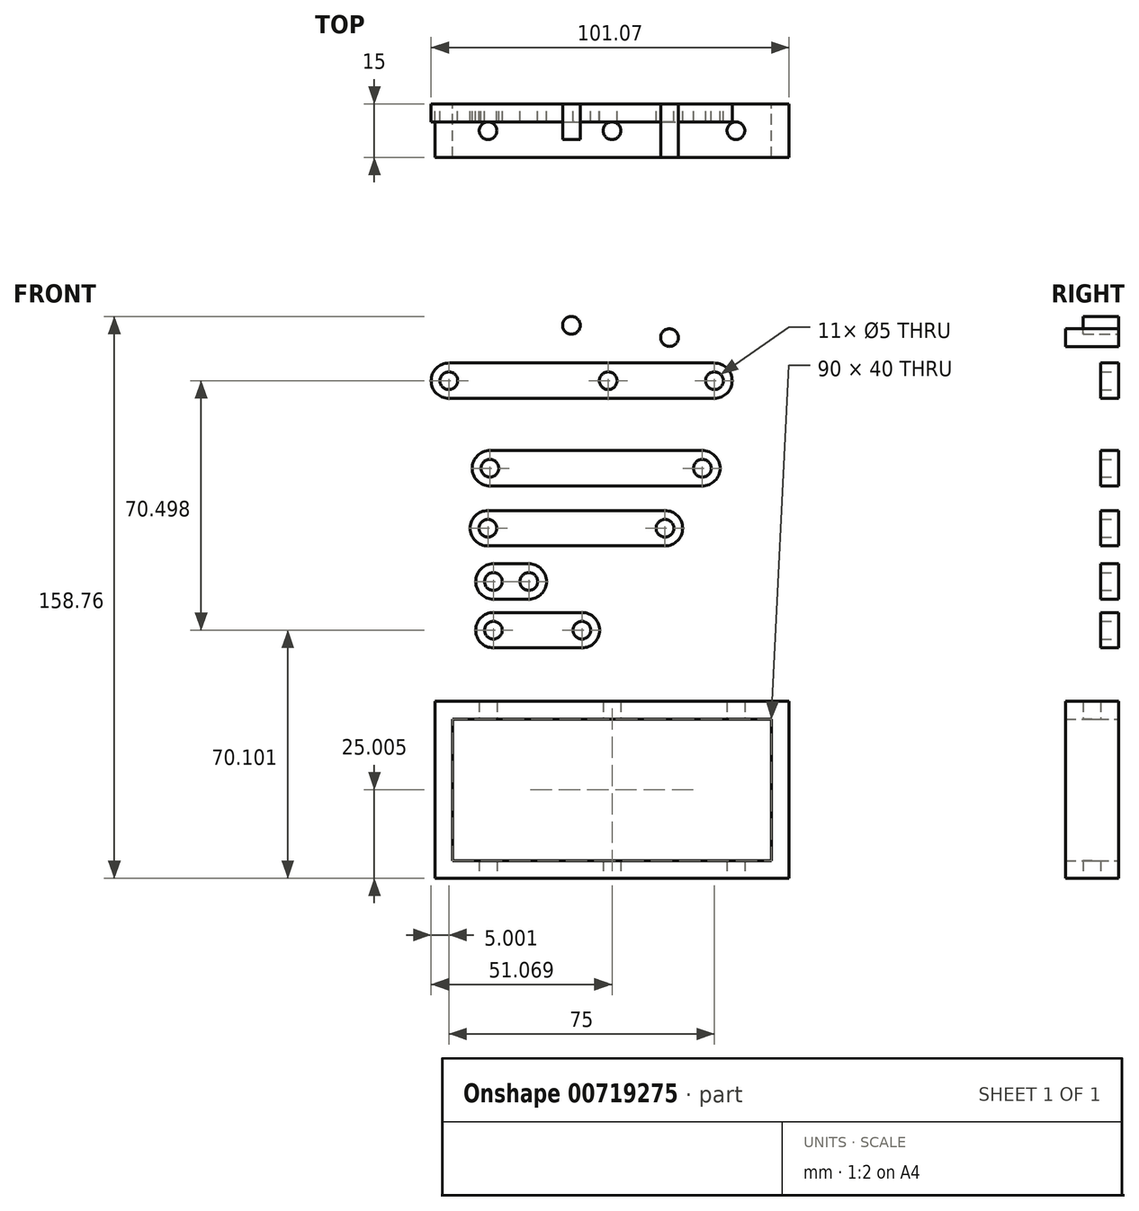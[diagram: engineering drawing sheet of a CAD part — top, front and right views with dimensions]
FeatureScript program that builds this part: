
annotation { "Feature Type Name" : "Feature", "Feature Type Description" : "" }
export const myFeature = defineFeature(function(context is Context, id is Id, definition is map)
    precondition{}
    {
        {
            assignVariable(context, id + "F0", {"name" : "thick", "anyValue" : 5});
        }
        {
            var Q0;
            Q0=qCreatedBy(makeId("Front.planeOp"),FACE);
            var sketch = newSketch(context, id + "F1", { "sketchPlane" : qUnion([Q0])});
            skArc(sketch, "E0", {"start": v(0, 5) * mm, "mid": v(-5, 0) * mm, "end": v(0, -5) * mm});
            skArc(sketch, "E1", {"start": v(10, -5) * mm, "mid": v(15, 0) * mm, "end": v(10, 5) * mm});
            skLineSegment(sketch, "E2", {"start": v(0, 5) * mm, "end": v(10, 5) * mm});
            skLineSegment(sketch, "E3", {"start": v(0, -5) * mm, "end": v(10, -5) * mm});
            skCircle(sketch, "E4", {"center": v(0, 0) * mm, "radius": 2.5 * mm});
            skCircle(sketch, "E5", {"center": v(10, 0) * mm, "radius": 2.5 * mm});
            skSolve(sketch);
        }
        {
            var Q0;
            Q0=makeQuery(id+"F1.imprint","IMPRINT",FACE,{"disambiguationData":[TD([[makeQuery(id+"F1.imprint","IMPRINT",EDGE,{"derivedFrom":sQuery(id+"F1.wireOp",EDGE,"E0")}),1.0]])]});
            extrude(context, id + "F2", {"entities" : qUnion([Q0]), "depth" : (getVariable(context, 'thick')) * mm, "offsetDistance" : 25 * mm});
        }
        {
            var Q0;
            Q0=qCreatedBy(makeId("Front.planeOp"),FACE);
            var sketch = newSketch(context, id + "F3", { "sketchPlane" : qUnion([Q0])});
            skArc(sketch, "E6", {"start": v(0, -8.76) * mm, "mid": v(-5, -13.76) * mm, "end": v(0, -18.76) * mm});
            skArc(sketch, "E7", {"start": v(25, -18.76) * mm, "mid": v(30, -13.76) * mm, "end": v(25, -8.76) * mm});
            skLineSegment(sketch, "E8", {"start": v(0, -8.76) * mm, "end": v(25, -8.76) * mm});
            skLineSegment(sketch, "E9", {"start": v(0, -18.76) * mm, "end": v(25, -18.76) * mm});
            skCircle(sketch, "E10", {"center": v(0, -13.76) * mm, "radius": 2.5 * mm});
            skCircle(sketch, "E11", {"center": v(25, -13.76) * mm, "radius": 2.5 * mm});
            skSolve(sketch);
        }
        {
            var Q0;
            Q0=makeQuery(id+"F3.imprint","IMPRINT",FACE,{"disambiguationData":[TD([[makeQuery(id+"F3.imprint","IMPRINT",EDGE,{"derivedFrom":sQuery(id+"F3.wireOp",EDGE,"E6")}),1.0]])]});
            extrude(context, id + "F4", {"entities" : qUnion([Q0]), "depth" : (getVariable(context, 'thick')) * mm, "offsetDistance" : 25 * mm});
        }
        {
            var Q0;
            Q0=qCreatedBy(makeId("Front.planeOp"),FACE);
            var sketch = newSketch(context, id + "F5", { "sketchPlane" : qUnion([Q0])});
            skArc(sketch, "E12", {"start": v(-1.55, 20.05) * mm, "mid": v(-6.55, 15.05) * mm, "end": v(-1.55, 10.05) * mm});
            skArc(sketch, "E13", {"start": v(48.45, 10.05) * mm, "mid": v(53.45, 15.05) * mm, "end": v(48.45, 20.05) * mm});
            skLineSegment(sketch, "E14", {"start": v(-1.55, 20.05) * mm, "end": v(48.45, 20.05) * mm});
            skLineSegment(sketch, "E15", {"start": v(-1.55, 10.05) * mm, "end": v(48.45, 10.05) * mm});
            skCircle(sketch, "E16", {"center": v(-1.55, 15.05) * mm, "radius": 2.5 * mm});
            skCircle(sketch, "E17", {"center": v(48.45, 15.05) * mm, "radius": 2.5 * mm});
            skSolve(sketch);
        }
        {
            var Q0;
            Q0=makeQuery(id+"F5.imprint","IMPRINT",FACE,{"disambiguationData":[TD([[makeQuery(id+"F5.imprint","IMPRINT",EDGE,{"derivedFrom":sQuery(id+"F5.wireOp",EDGE,"E12")}),1.0]])]});
            extrude(context, id + "F6", {"entities" : qUnion([Q0]), "depth" : (getVariable(context, 'thick')) * mm, "offsetDistance" : 25 * mm});
        }
        {
            var Q0;
            Q0=qCreatedBy(makeId("Front.planeOp"),FACE);
            var sketch = newSketch(context, id + "F7", { "sketchPlane" : qUnion([Q0])});
            skArc(sketch, "E18", {"start": v(-0.99, 37) * mm, "mid": v(-5.99, 32) * mm, "end": v(-0.99, 27) * mm});
            skArc(sketch, "E19", {"start": v(59.01, 27) * mm, "mid": v(64.01, 32) * mm, "end": v(59.01, 37) * mm});
            skLineSegment(sketch, "E20", {"start": v(-0.99, 37) * mm, "end": v(59.01, 37) * mm});
            skLineSegment(sketch, "E21", {"start": v(-0.99, 27) * mm, "end": v(59.01, 27) * mm});
            skCircle(sketch, "E22", {"center": v(-0.99, 32) * mm, "radius": 2.5 * mm});
            skCircle(sketch, "E23", {"center": v(59.01, 32) * mm, "radius": 2.5 * mm});
            skSolve(sketch);
        }
        {
            var Q0;
            Q0=makeQuery(id+"F7.imprint","IMPRINT",FACE,{"disambiguationData":[TD([[makeQuery(id+"F7.imprint","IMPRINT",EDGE,{"derivedFrom":sQuery(id+"F7.wireOp",EDGE,"E18")}),1.0]])]});
            extrude(context, id + "F8", {"entities" : qUnion([Q0]), "depth" : (getVariable(context, 'thick')) * mm, "offsetDistance" : 25 * mm});
        }
        {
            var Q0;
            Q0=qCreatedBy(makeId("Front.planeOp"),FACE);
            var sketch = newSketch(context, id + "F9", { "sketchPlane" : qUnion([Q0])});
            skArc(sketch, "E24", {"start": v(-12.58, 61.74) * mm, "mid": v(-17.58, 56.74) * mm, "end": v(-12.58, 51.74) * mm});
            skArc(sketch, "E25", {"start": v(62.42, 51.74) * mm, "mid": v(67.42, 56.74) * mm, "end": v(62.42, 61.74) * mm});
            skLineSegment(sketch, "E26", {"start": v(-12.58, 61.74) * mm, "end": v(62.42, 61.74) * mm});
            skLineSegment(sketch, "E27", {"start": v(-12.58, 51.74) * mm, "end": v(62.42, 51.74) * mm});
            skCircle(sketch, "E28", {"center": v(-12.58, 56.74) * mm, "radius": 2.5 * mm});
            skCircle(sketch, "E29", {"center": v(62.42, 56.74) * mm, "radius": 2.5 * mm});
            skCircle(sketch, "E30", {"center": v(32.42, 56.74) * mm, "radius": 2.5 * mm});
            skSolve(sketch);
        }
        {
            var Q0;
            Q0=makeQuery(id+"F9.imprint","IMPRINT",FACE,{"disambiguationData":[TD([[makeQuery(id+"F9.imprint","IMPRINT",EDGE,{"derivedFrom":sQuery(id+"F9.wireOp",EDGE,"E24")}),1.0]])]});
            extrude(context, id + "F10", {"entities" : qUnion([Q0]), "depth" : (getVariable(context, 'thick')) * mm, "offsetDistance" : 25 * mm});
        }
        {
            var Q0;
            Q0=qCreatedBy(makeId("Front.planeOp"),FACE);
            var sketch = newSketch(context, id + "F11", { "sketchPlane" : qUnion([Q0])});
            skLineSegment(sketch, "E31.bottom", {"start": v(-16.51, -33.86) * mm, "end": v(83.49, -33.86) * mm});
            skLineSegment(sketch, "E31.top", {"start": v(-16.51, -83.86) * mm, "end": v(83.49, -83.86) * mm});
            skLineSegment(sketch, "E31.left", {"start": v(-16.51, -33.86) * mm, "end": v(-16.51, -83.86) * mm});
            skLineSegment(sketch, "E31.right", {"start": v(83.49, -33.86) * mm, "end": v(83.49, -83.86) * mm});
            skLineSegment(sketch, "E32.bottom", {"start": v(-11.51, -38.86) * mm, "end": v(78.49, -38.86) * mm});
            skLineSegment(sketch, "E32.top", {"start": v(-11.51, -78.86) * mm, "end": v(78.49, -78.86) * mm});
            skLineSegment(sketch, "E32.left", {"start": v(-11.51, -38.86) * mm, "end": v(-11.51, -78.86) * mm});
            skLineSegment(sketch, "E32.right", {"start": v(78.49, -38.86) * mm, "end": v(78.49, -78.86) * mm});
            skSolve(sketch);
        }
        {
            var Q0;
            Q0 = qSketchRegion(id + "F11", true);
            extrude(context, id + "F12", {"entities" : qUnion([Q0]), "depth" : 15 * mm, "offsetDistance" : 25 * mm});
        }
        {
            var Q0;
            Q0=makeQuery(id+"F12.opExtrude","SWEPT_FACE",FACE,{"disambiguationData":[OSD([sQuery(id+"F11.wireOp",EDGE,"E31.top")])]});
            var sketch = newSketch(context, id + "F13", { "sketchPlane" : qUnion([Q0])});
            skCircle(sketch, "E33", {"center": v(68.49, 7.5) * mm, "radius": 2.5 * mm});
            skCircle(sketch, "E34", {"center": v(33.49, 7.5) * mm, "radius": 2.5 * mm});
            skCircle(sketch, "E35", {"center": v(-1.51, 7.5) * mm, "radius": 2.5 * mm});
            skSolve(sketch);
        }
        {
            var Q0;
            Q0=makeQuery(id+"F13.imprint","IMPRINT",FACE,{"disambiguationData":[TD([[makeQuery(id+"F13.imprint","IMPRINT",EDGE,{"derivedFrom":sQuery(id+"F13.wireOp",EDGE,"E35")}),1.0]])]});
            var Q1;
            Q1=makeQuery(id+"F13.imprint","IMPRINT",FACE,{"disambiguationData":[TD([[makeQuery(id+"F13.imprint","IMPRINT",EDGE,{"derivedFrom":sQuery(id+"F13.wireOp",EDGE,"E34")}),1.0]])]});
            var Q2;
            Q2=makeQuery(id+"F13.imprint","IMPRINT",FACE,{"disambiguationData":[TD([[makeQuery(id+"F13.imprint","IMPRINT",EDGE,{"derivedFrom":sQuery(id+"F13.wireOp",EDGE,"E33")}),1.0]])]});
            extrude(context, id + "F14", {"entities" : qUnion([Q0, Q1, Q2]), "operationType" : NewBodyOperationType.REMOVE, "oppositeDirection" : true, "depth" : 50 * mm, "offsetDistance" : 25 * mm});
        }
        {
            var Q0;
            Q0=qCreatedBy(makeId("Front.planeOp"),FACE);
            var sketch = newSketch(context, id + "F15", { "sketchPlane" : qUnion([Q0])});
            skCircle(sketch, "E36", {"center": v(22.03, 72.4) * mm, "radius": 2.5 * mm});
            skSolve(sketch);
        }
        {
            var Q0;
            Q0=makeQuery(id+"F15.imprint","IMPRINT",FACE,{"disambiguationData":[TD([[makeQuery(id+"F15.imprint","IMPRINT",EDGE,{"derivedFrom":sQuery(id+"F15.wireOp",EDGE,"E36")}),1.0]])]});
            extrude(context, id + "F16", {"entities" : qUnion([Q0]), "depth" : 10 * mm, "offsetDistance" : 25 * mm});
        }
        {
            var Q0;
            Q0=qCreatedBy(makeId("Front.planeOp"),FACE);
            var sketch = newSketch(context, id + "F17", { "sketchPlane" : qUnion([Q0])});
            skCircle(sketch, "E37", {"center": v(49.72, 68.93) * mm, "radius": 2.5 * mm});
            skSolve(sketch);
        }
        {
            var Q0;
            Q0 = qSketchRegion(id + "F17", true);
            extrude(context, id + "F18", {"entities" : qUnion([Q0]), "depth" : 15 * mm, "offsetDistance" : 25 * mm});
        }
    });
